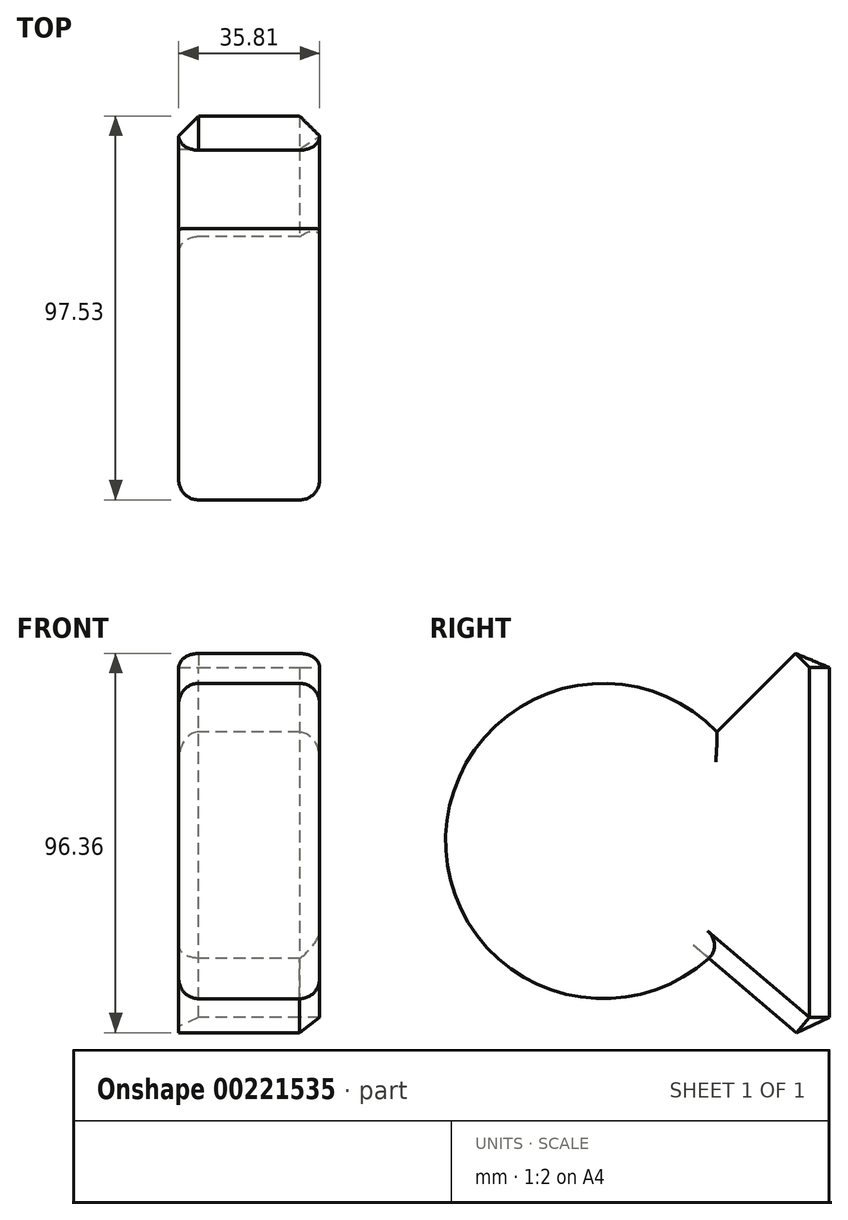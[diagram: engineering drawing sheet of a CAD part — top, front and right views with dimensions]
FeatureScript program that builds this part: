
annotation { "Feature Type Name" : "Feature", "Feature Type Description" : "" }
export const myFeature = defineFeature(function(context is Context, id is Id, definition is map)
    precondition{}
    {
        {
            var Q0;
            Q0=qCreatedBy(makeId("Right.planeOp"),FACE);
            var sketch = newSketch(context, id + "F0", { "sketchPlane" : qUnion([Q0])});
            skCircle(sketch, "E0", {"center": v(0, 0) * mm, "radius": 40.05 * mm});
            skLineSegment(sketch, "E1", {"start": v(28.93, 27.7) * mm, "end": v(57.48, 56.4) * mm});
            skLineSegment(sketch, "E2", {"start": v(57.48, 56.4) * mm, "end": v(57.48, -55.77) * mm});
            skLineSegment(sketch, "E3", {"start": v(57.48, -55.77) * mm, "end": v(26.8, -29.76) * mm});
            skSolve(sketch);
        }
        {
            var Q0;
            Q0 = qSketchRegion(id + "F0", true);
            var Q1;
            {var subQ0=sQuery(id+"F0.wireOp",EDGE,"E0");var subQ1=makeQuery(id+"F0.imprint","INTERSECT",VERTEX,{"derivedFrom":[subQ0,sQuery(id+"F0.wireOp",EDGE,"E1")]});Q1=makeQuery(id+"F0.imprint","IMPRINT",FACE,{"disambiguationData":[TD([[makeQuery(id+"F0.imprint","IMPRINT",EDGE,{"disambiguationData":[TD([[subQ1,-1.0]])],"derivedFrom":subQ0}),1.0]])]});}
            extrude(context, id + "F1", {"entities" : qUnion([Q0, Q1]), "depth" : 35.81 * mm});
        }
        {
            var Q0;
            Q0=makeQuery(id+"F1.opExtrude","CAP_EDGE",EDGE,{"disambiguationData":[OSD([sQuery(id+"F0.wireOp",EDGE,"E0")])],"isStart":false});
            var Q1;
            Q1=makeQuery(id+"F1.opExtrude","CAP_EDGE",EDGE,{"disambiguationData":[OSD([sQuery(id+"F0.wireOp",EDGE,"E0")])],"isStart":true});
            var Q2;
            Q2=makeQuery(id+"F1.opExtrude","CAP_EDGE",EDGE,{"disambiguationData":[OSD([sQuery(id+"F0.wireOp",EDGE,"E1")])],"isStart":false});
            var Q3;
            Q3=makeQuery(id+"F1.opExtrude","CAP_EDGE",EDGE,{"disambiguationData":[OSD([sQuery(id+"F0.wireOp",EDGE,"E1")])],"isStart":true});
            fillet(context, id + "F2", {"entities" : qUnion([Q0, Q1, Q2, Q3]), "radius" : 5.08 * mm, "tangentPropagation" : true, "allowEdgeOverflow" : false});
        }
        {
            var Q0;
            Q0=makeQuery(id+"F1.opExtrude","SWEPT_EDGE",EDGE,{"disambiguationData":[OSD([sQuery(id+"F0.wireOp",EDGE,"E1"),sQuery(id+"F0.wireOp",EDGE,"E2")])]});
            var Q1;
            Q1=makeQuery(id+"F1.opExtrude","CAP_EDGE",EDGE,{"disambiguationData":[OSD([sQuery(id+"F0.wireOp",EDGE,"E2")])],"isStart":false});
            var Q2;
            Q2=makeQuery(id+"F1.opExtrude","CAP_EDGE",EDGE,{"disambiguationData":[OSD([sQuery(id+"F0.wireOp",EDGE,"E3")])],"isStart":false});
            var Q3;
            {var subQ0=sQuery(id+"F0.wireOp",EDGE,"E1");Q3=makeQuery(id+"F2.opFillet","BLEND_EDGE",EDGE,{"blendedFrom":[makeQuery(id+"F1.opExtrude","CAP_EDGE",EDGE,{"disambiguationData":[OSD([subQ0])],"isStart":true}),makeQuery(id+"F1.opExtrude","CAP_FACE",FACE,{"disambiguationData":[OSD([sQuery(id+"F0.wireOp",EDGE,"E0"),subQ0,sQuery(id+"F0.wireOp",EDGE,"E2"),sQuery(id+"F0.wireOp",EDGE,"E3")])],"isStart":true})],"blendedInto":[makeQuery(id+"F1.opExtrude","CAP_FACE",FACE,{"disambiguationData":[OSD([sQuery(id+"F0.wireOp",EDGE,"E0"),subQ0,sQuery(id+"F0.wireOp",EDGE,"E2"),sQuery(id+"F0.wireOp",EDGE,"E3")])],"isStart":true})]});}
            var Q4;
            Q4=makeQuery(id+"F1.opExtrude","SWEPT_EDGE",EDGE,{"disambiguationData":[OSD([sQuery(id+"F0.wireOp",EDGE,"E2"),sQuery(id+"F0.wireOp",EDGE,"E3")])]});
            chamfer(context, id + "F3", {"entities" : qUnion([Q0, Q1, Q2, Q3, Q4]), "width" : 5.08 * mm, "tangentPropagation" : true});
        }
    });
